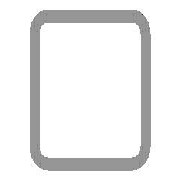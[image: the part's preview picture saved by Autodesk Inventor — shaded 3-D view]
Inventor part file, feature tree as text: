
AUTODESK INVENTOR PART (.ipt)
format: ipt  version: 2025 (Build 290162010, 162A)  size: 134,144 bytes
history: native  units: mm (DEFAULTED — no unit token found)
features: other x4, sketch x1, plane x1
ambient origin geometry x8: Origin, YZ Plane, XZ Plane, XY Plane, X Axis, Y Axis, Z Axis, Center Point
bodies: Solid1 (feature_tree), Body (feature_tree)
feature tree (6):
  parser-record x1  (decoder bookkeeping rows leaked as tree rows — omitted from the tree; the rows remain in map.json)
  other  "Driven Length"
  other  "Start Plane"
  other  "End Plane"
  sketch  "Sketch3"  dims[d3=1420.0mm d4=0.0mm d7=4.0mm d9=40.0mm d11=40.0mm d12=2.0mm d13=40.0mm d14=1460.0mm d15=20.0mm d16=20.0mm d17=90.0deg d18=1420.0mm]
  plane  "Work Plane3"
